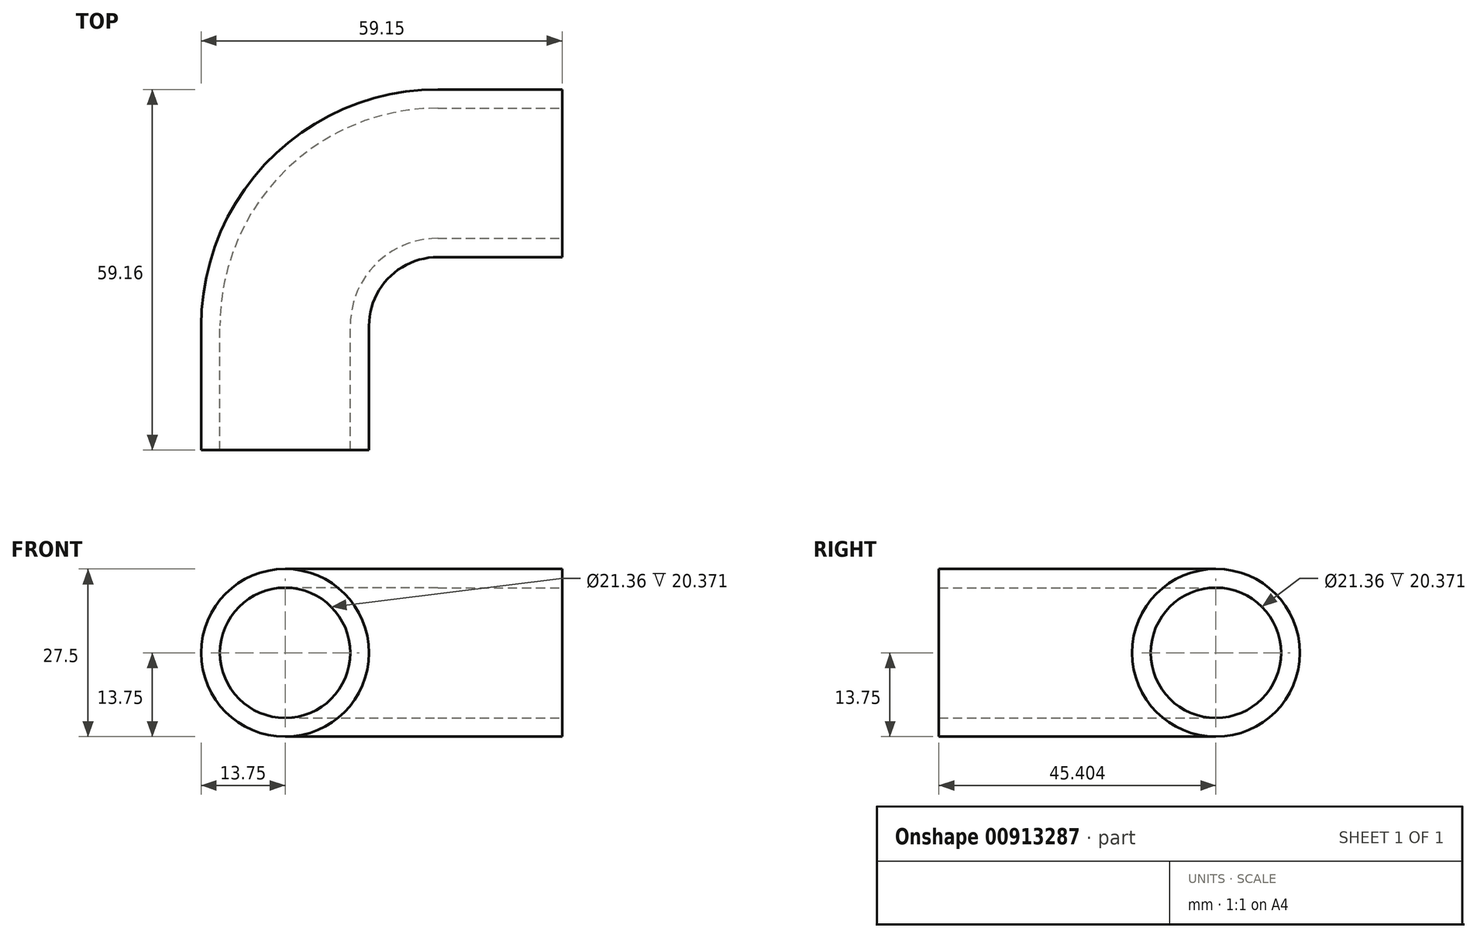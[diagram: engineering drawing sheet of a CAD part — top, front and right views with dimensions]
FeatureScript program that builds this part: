
annotation { "Feature Type Name" : "Feature", "Feature Type Description" : "" }
export const myFeature = defineFeature(function(context is Context, id is Id, definition is map)
    precondition{}
    {
        {
            var Q0;
            Q0=qCreatedBy(makeId("Front.planeOp"),FACE);
            cPlane(context, id + "F0", {"entities" : qUnion([Q0]), "cplaneType" : CPlaneType.OFFSET, "offset" : 31.65 * mm, "width" : 152.4 * mm, "height" : 152.4 * mm});
        }
        {
            var Q0;
            Q0=qCreatedBy(id+"F0.planeOp",FACE);
            var sketch = newSketch(context, id + "F1", { "sketchPlane" : qUnion([Q0])});
            skCircle(sketch, "E0", {"center": v(0, 0) * mm, "radius": 13.75 * mm});
            skCircle(sketch, "E1", {"center": v(0, 0) * mm, "radius": 10.68 * mm});
            skSolve(sketch);
        }
        {
            var Q0;
            Q0=qCreatedBy(makeId("Top.planeOp"),FACE);
            var sketch = newSketch(context, id + "F2", { "sketchPlane" : qUnion([Q0])});
            skPoint(sketch, "E2.0", {"position": v(0, -31.65) * mm});
            skLineSegment(sketch, "E3", {"start": v(0, -31.65) * mm, "end": v(0, -11.28) * mm});
            skLineSegment(sketch, "E4", {"start": v(25.03, 13.75) * mm, "end": v(45.4, 13.75) * mm});
            skPoint(sketch, "E5.visualSharp", {"position": v(0, 13.75) * mm});
            skArc(sketch, "E5.filletArc", {"start": v(25.03, 13.75) * mm, "mid": v(7.33, 6.42) * mm, "end": v(0, -11.28) * mm});
            skSolve(sketch);
        }
        {
            var Q0;
            Q0=makeQuery(id+"F1.imprint","IMPRINT",FACE,{"disambiguationData":[TD([[makeQuery(id+"F1.imprint","IMPRINT",EDGE,{"derivedFrom":sQuery(id+"F1.wireOp",EDGE,"E0")}),1.0]])]});
            var Q1;
            Q1=sQuery(id+"F2.wireOp",EDGE,"E5.filletArc");
            var Q2;
            Q2=sQuery(id+"F2.wireOp",EDGE,"E3");
            var Q3;
            Q3=sQuery(id+"F2.wireOp",EDGE,"E4");
            sweep(context, id + "F3", {"profiles" : qUnion([Q0]), "path" : qUnion([Q1, Q2, Q3])});
        }
    });
